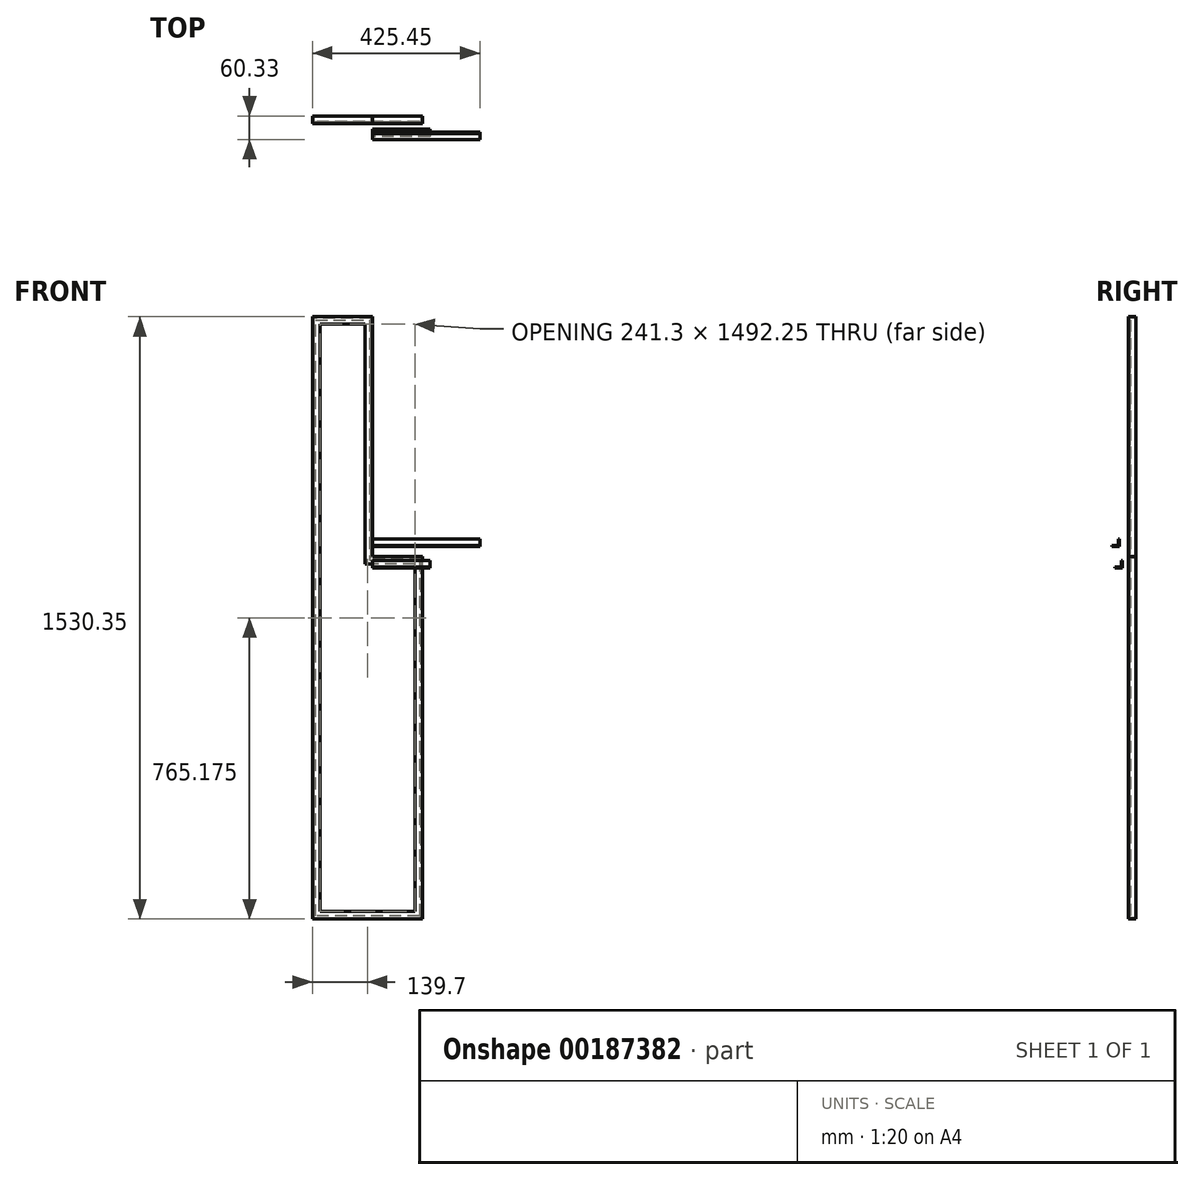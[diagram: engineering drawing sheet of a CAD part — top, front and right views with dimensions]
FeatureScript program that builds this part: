
annotation { "Feature Type Name" : "Feature", "Feature Type Description" : "" }
export const myFeature = defineFeature(function(context is Context, id is Id, definition is map)
    precondition{}
    {
        {
            var Q0;
            Q0=qCreatedBy(makeId("Front.planeOp"),FACE);
            var sketch = newSketch(context, id + "F0", { "sketchPlane" : qUnion([Q0])});
            skLineSegment(sketch, "E0", {"start": v(0, 609.6) * mm, "end": v(-152.4, 609.6) * mm});
            skLineSegment(sketch, "E1", {"start": v(-152.4, 609.6) * mm, "end": v(-152.4, -920.75) * mm});
            skLineSegment(sketch, "E2", {"start": v(-152.4, -920.75) * mm, "end": v(127, -920.75) * mm});
            skLineSegment(sketch, "E3", {"start": v(127, -920.75) * mm, "end": v(127, 0) * mm});
            skLineSegment(sketch, "E4", {"start": v(127, 0) * mm, "end": v(0, 0) * mm});
            skLineSegment(sketch, "E5", {"start": v(0, 0) * mm, "end": v(0, 609.6) * mm});
            skLineSegment(sketch, "E6.0", {"start": v(-19.05, 590.55) * mm, "end": v(-133.35, 590.55) * mm});
            skLineSegment(sketch, "E6.1", {"start": v(-133.35, -901.7) * mm, "end": v(107.95, -901.7) * mm});
            skLineSegment(sketch, "E6.2", {"start": v(107.95, -901.7) * mm, "end": v(107.95, -19.05) * mm});
            skLineSegment(sketch, "E6.3", {"start": v(-133.35, 590.55) * mm, "end": v(-133.35, -901.7) * mm});
            skLineSegment(sketch, "E6.4", {"start": v(107.95, -19.05) * mm, "end": v(-19.05, -19.05) * mm});
            skLineSegment(sketch, "E6.5", {"start": v(-19.05, -19.05) * mm, "end": v(-19.05, 590.55) * mm});
            skSolve(sketch);
        }
        {
            var Q0;
            Q0=makeQuery(id+"F0.imprint","IMPRINT",FACE,{"disambiguationData":[TD([[makeQuery(id+"F0.imprint","IMPRINT",EDGE,{"derivedFrom":sQuery(id+"F0.wireOp",EDGE,"E0")}),1.0]])]});
            extrude(context, id + "F1", {"entities" : qUnion([Q0]), "depth" : 3.17 * mm});
        }
        {
            var Q0;
            Q0=makeQuery(id+"F1.opExtrude","CAP_FACE",FACE,{"disambiguationData":[OSD([sQuery(id+"F0.wireOp",EDGE,"E0"),sQuery(id+"F0.wireOp",EDGE,"E1"),sQuery(id+"F0.wireOp",EDGE,"E2"),sQuery(id+"F0.wireOp",EDGE,"E3"),sQuery(id+"F0.wireOp",EDGE,"E4"),sQuery(id+"F0.wireOp",EDGE,"E5"),sQuery(id+"F0.wireOp",EDGE,"E6.0"),sQuery(id+"F0.wireOp",EDGE,"E6.1"),sQuery(id+"F0.wireOp",EDGE,"E6.2"),sQuery(id+"F0.wireOp",EDGE,"E6.3"),sQuery(id+"F0.wireOp",EDGE,"E6.4"),sQuery(id+"F0.wireOp",EDGE,"E6.5")])],"isStart":true});
            var sketch = newSketch(context, id + "F2", { "sketchPlane" : qUnion([Q0])});
            skLineSegment(sketch, "E7.0", {"start": v(-123.83, -3.18) * mm, "end": v(3.17, -3.18) * mm});
            skLineSegment(sketch, "E7.1", {"start": v(3.17, 606.42) * mm, "end": v(149.22, 606.42) * mm});
            skLineSegment(sketch, "E7.2", {"start": v(149.22, 606.42) * mm, "end": v(149.22, -917.57) * mm});
            skLineSegment(sketch, "E7.3", {"start": v(3.18, -3.18) * mm, "end": v(3.18, 606.42) * mm});
            skLineSegment(sketch, "E7.4", {"start": v(149.22, -917.57) * mm, "end": v(-123.83, -917.57) * mm});
            skLineSegment(sketch, "E7.5", {"start": v(-123.83, -917.57) * mm, "end": v(-123.83, -3.18) * mm});
            skSolve(sketch);
        }
        {
            var Q0;
            Q0=makeQuery(id+"F2.imprint","IMPRINT",FACE,{"disambiguationData":[TD([[makeQuery(id+"F2.imprint","IMPRINT",EDGE,{"derivedFrom":sQuery(id+"F2.wireOp",EDGE,"E7.0")}),1.0]])]});
            extrude(context, id + "F3", {"entities" : qUnion([Q0]), "operationType" : NewBodyOperationType.ADD, "depth" : 15.88 * mm});
        }
        {
            var Q0;
            Q0=qCreatedBy(makeId("Right.planeOp"),FACE);
            var sketch = newSketch(context, id + "F4", { "sketchPlane" : qUnion([Q0])});
            skLineSegment(sketch, "E8", {"start": v(-25.4, 44.45) * mm, "end": v(-25.4, 25.4) * mm});
            skLineSegment(sketch, "E9", {"start": v(-25.4, 25.4) * mm, "end": v(-44.45, 25.4) * mm});
            skLineSegment(sketch, "E10", {"start": v(-44.45, 25.4) * mm, "end": v(-44.45, 28.57) * mm});
            skLineSegment(sketch, "E11", {"start": v(-44.45, 28.57) * mm, "end": v(-28.58, 28.57) * mm});
            skLineSegment(sketch, "E12", {"start": v(-28.58, 28.57) * mm, "end": v(-28.58, 44.45) * mm});
            skLineSegment(sketch, "E13", {"start": v(-28.58, 44.45) * mm, "end": v(-25.4, 44.45) * mm});
            skSolve(sketch);
        }
        {
            var Q0;
            Q0=makeQuery(id+"F4.imprint","IMPRINT",FACE,{"disambiguationData":[TD([[makeQuery(id+"F4.imprint","IMPRINT",EDGE,{"derivedFrom":sQuery(id+"F4.wireOp",EDGE,"E8")}),-1.0]])]});
            extrude(context, id + "F5", {"entities" : qUnion([Q0]), "depth" : 273.05 * mm});
        }
        {
            var Q0;
            Q0=qCreatedBy(makeId("Right.planeOp"),FACE);
            var sketch = newSketch(context, id + "F6", { "sketchPlane" : qUnion([Q0])});
            skLineSegment(sketch, "E14", {"start": v(-17.96, -10.13) * mm, "end": v(-17.96, -29.18) * mm});
            skLineSegment(sketch, "E15", {"start": v(-17.96, -29.18) * mm, "end": v(-37.01, -29.18) * mm});
            skLineSegment(sketch, "E16", {"start": v(-37.01, -29.18) * mm, "end": v(-37.01, -26) * mm});
            skLineSegment(sketch, "E17", {"start": v(-37.01, -26) * mm, "end": v(-21.14, -26) * mm});
            skLineSegment(sketch, "E18", {"start": v(-21.14, -26) * mm, "end": v(-21.14, -10.13) * mm});
            skLineSegment(sketch, "E19", {"start": v(-21.14, -10.13) * mm, "end": v(-17.96, -10.13) * mm});
            skSolve(sketch);
        }
        {
            var Q0;
            Q0=makeQuery(id+"F6.imprint","IMPRINT",FACE,{"disambiguationData":[TD([[makeQuery(id+"F6.imprint","IMPRINT",EDGE,{"derivedFrom":sQuery(id+"F6.wireOp",EDGE,"E14")}),-1.0]])]});
            extrude(context, id + "F7", {"entities" : qUnion([Q0]), "depth" : 146.05 * mm});
        }
        {
            var Q0;
            Q0=makeQuery(id+"F1.opExtrude","CAP_FACE",FACE,{"disambiguationData":[OSD([sQuery(id+"F0.wireOp",EDGE,"E0"),sQuery(id+"F0.wireOp",EDGE,"E1"),sQuery(id+"F0.wireOp",EDGE,"E2"),sQuery(id+"F0.wireOp",EDGE,"E3"),sQuery(id+"F0.wireOp",EDGE,"E4"),sQuery(id+"F0.wireOp",EDGE,"E5"),sQuery(id+"F0.wireOp",EDGE,"E6.0"),sQuery(id+"F0.wireOp",EDGE,"E6.1"),sQuery(id+"F0.wireOp",EDGE,"E6.2"),sQuery(id+"F0.wireOp",EDGE,"E6.3"),sQuery(id+"F0.wireOp",EDGE,"E6.4"),sQuery(id+"F0.wireOp",EDGE,"E6.5")])],"isStart":true});
            var sketch = newSketch(context, id + "F8", { "sketchPlane" : qUnion([Q0])});
            skLineSegment(sketch, "E20.0.0", {"start": v(-123.83, -3.18) * mm, "end": v(-123.83, -917.57) * mm});
            skLineSegment(sketch, "E20.0.1", {"start": v(-123.83, -917.57) * mm, "end": v(149.22, -917.57) * mm});
            skLineSegment(sketch, "E20.0.2", {"start": v(149.22, -917.57) * mm, "end": v(149.22, 606.42) * mm});
            skLineSegment(sketch, "E20.0.3", {"start": v(149.22, 606.42) * mm, "end": v(3.17, 606.42) * mm});
            skLineSegment(sketch, "E20.0.4", {"start": v(3.18, 606.42) * mm, "end": v(3.18, -3.18) * mm});
            skLineSegment(sketch, "E20.0.5", {"start": v(3.17, -3.18) * mm, "end": v(-123.83, -3.18) * mm});
            skLineSegment(sketch, "E21.0", {"start": v(7.94, -7.94) * mm, "end": v(-119.06, -7.94) * mm});
            skLineSegment(sketch, "E21.1", {"start": v(-119.06, -912.81) * mm, "end": v(144.46, -912.81) * mm});
            skLineSegment(sketch, "E21.2", {"start": v(144.46, -912.81) * mm, "end": v(144.46, 601.66) * mm});
            skLineSegment(sketch, "E21.3", {"start": v(-119.06, -7.94) * mm, "end": v(-119.06, -912.81) * mm});
            skLineSegment(sketch, "E21.4", {"start": v(144.46, 601.66) * mm, "end": v(7.94, 601.66) * mm});
            skLineSegment(sketch, "E21.5", {"start": v(7.94, 601.66) * mm, "end": v(7.94, -7.94) * mm});
            skSolve(sketch);
        }
        {
            var Q0;
            Q0=makeQuery(id+"F8.imprint","IMPRINT",FACE,{"disambiguationData":[TD([[makeQuery(id+"F8.imprint","IMPRINT",EDGE,{"derivedFrom":sQuery(id+"F8.wireOp",EDGE,"E21.0")}),1.0]])]});
            var Q1;
            Q1=makeQuery(id+"F8.imprint","IMPRINT",FACE,{"disambiguationData":[TD([[makeQuery(id+"F8.imprint","IMPRINT",EDGE,{"derivedFrom":makeQuery(id+"F1.opExtrude","CAP_EDGE",EDGE,{"disambiguationData":[OSD([sQuery(id+"F0.wireOp",EDGE,"E6.0")])],"isStart":true})}),-1.0]])]});
            extrude(context, id + "F9", {"entities" : qUnion([Q0, Q1]), "depth" : 1.59 * mm});
        }
    });
